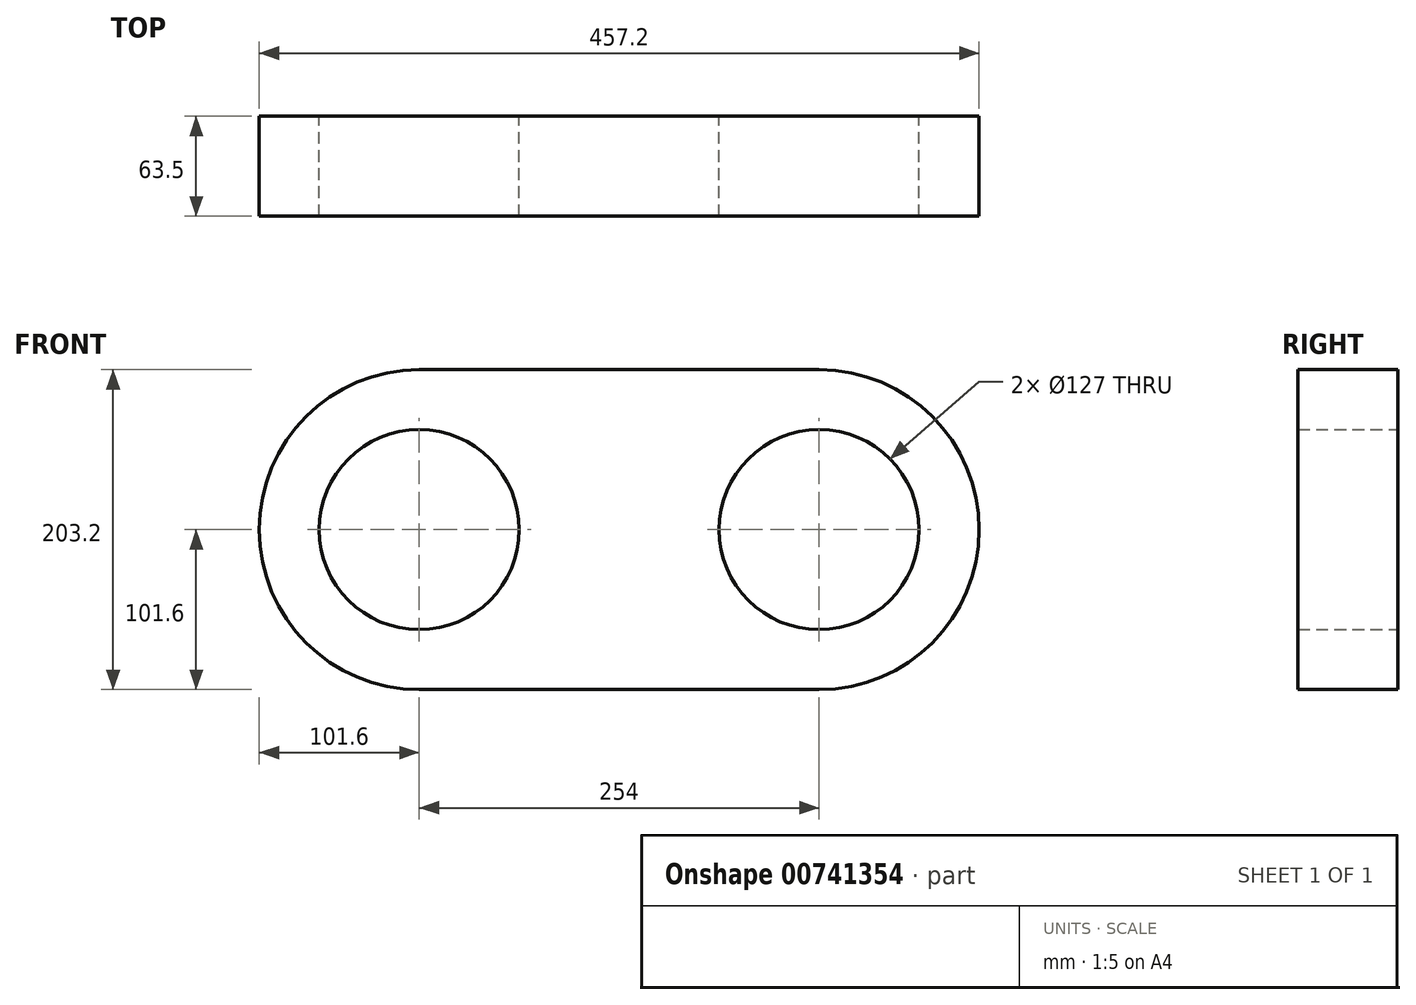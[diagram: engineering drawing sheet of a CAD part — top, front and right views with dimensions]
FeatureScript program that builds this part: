
annotation { "Feature Type Name" : "Feature", "Feature Type Description" : "" }
export const myFeature = defineFeature(function(context is Context, id is Id, definition is map)
    precondition{}
    {
        {
            var Q0;
            Q0=qCreatedBy(makeId("Front.planeOp"),FACE);
            var sketch = newSketch(context, id + "F0", { "sketchPlane" : qUnion([Q0])});
            skArc(sketch, "E0", {"start": v(-127, 101.6) * mm, "mid": v(-228.6, 0) * mm, "end": v(-127, -101.6) * mm});
            skArc(sketch, "E1", {"start": v(127, -101.6) * mm, "mid": v(228.6, 0) * mm, "end": v(127, 101.6) * mm});
            skLineSegment(sketch, "E2", {"start": v(-127, 101.6) * mm, "end": v(127, 101.6) * mm});
            skLineSegment(sketch, "E3", {"start": v(127, -101.6) * mm, "end": v(-127, -101.6) * mm});
            skCircle(sketch, "E4", {"center": v(127, 0) * mm, "radius": 63.5 * mm});
            skCircle(sketch, "E5", {"center": v(-127, 0) * mm, "radius": 63.5 * mm});
            skSolve(sketch);
        }
        {
            var Q0;
            Q0 = qSketchRegion(id + "F0", true);
            extrude(context, id + "F1", {"entities" : qUnion([Q0]), "endBound" : BoundingType.SYMMETRIC, "depth" : 63.5 * mm, "offsetDistance" : 25.4 * mm});
        }
    });
